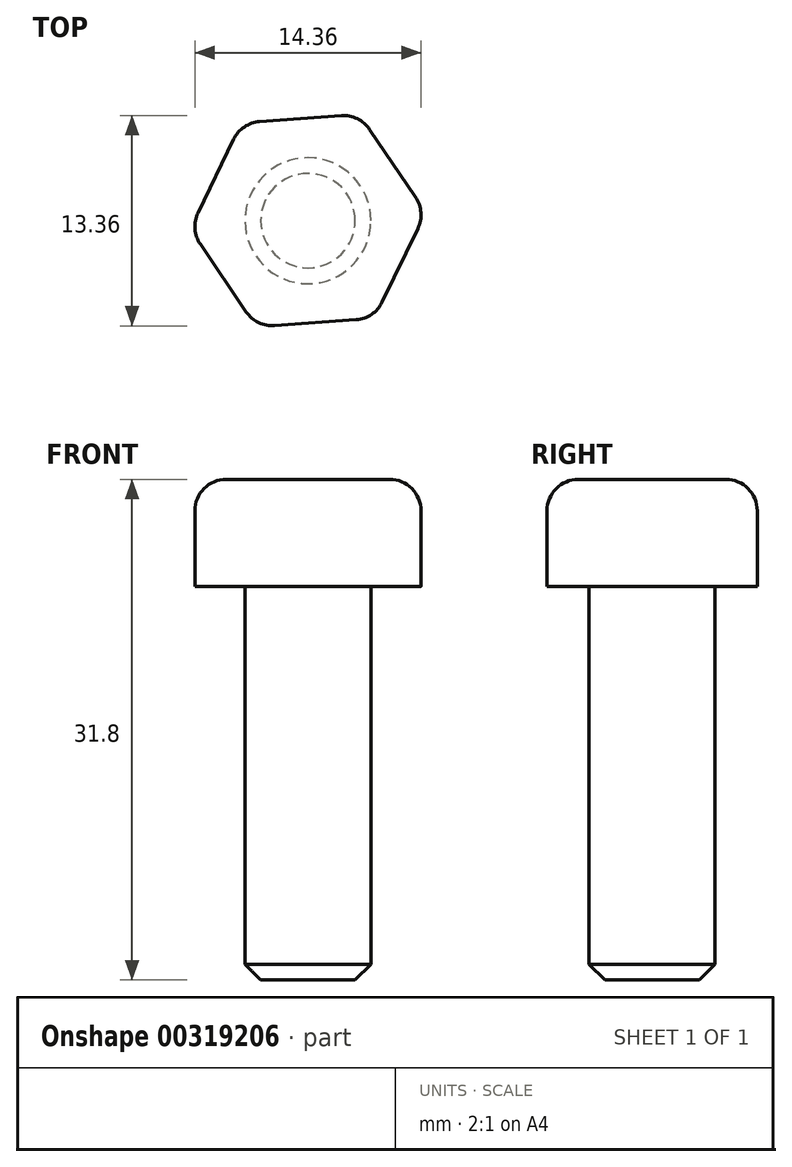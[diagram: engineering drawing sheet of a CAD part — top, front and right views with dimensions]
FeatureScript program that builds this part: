
annotation { "Feature Type Name" : "Feature", "Feature Type Description" : "" }
export const myFeature = defineFeature(function(context is Context, id is Id, definition is map)
    precondition{}
    {
        {
            var Q0;
            Q0=qCreatedBy(makeId("Top.planeOp"),FACE);
            var sketch = newSketch(context, id + "F0", { "sketchPlane" : qUnion([Q0])});
            skCircle(sketch, "E0.cCircle", {"center": v(0, 0) * mm, "radius": 6.5 * mm, "construction": true});
            skLineSegment(sketch, "E0.0", {"start": v(3.27, 6.76) * mm, "end": v(7.49, 0.54) * mm});
            skLineSegment(sketch, "E0.1", {"start": v(7.49, 0.54) * mm, "end": v(4.21, -6.21) * mm});
            skLineSegment(sketch, "E0.2", {"start": v(4.21, -6.21) * mm, "end": v(-3.27, -6.76) * mm});
            skLineSegment(sketch, "E0.3", {"start": v(-3.27, -6.76) * mm, "end": v(-7.49, -0.54) * mm});
            skLineSegment(sketch, "E0.4", {"start": v(-7.49, -0.54) * mm, "end": v(-4.21, 6.21) * mm});
            skLineSegment(sketch, "E0.5", {"start": v(-4.21, 6.21) * mm, "end": v(3.27, 6.76) * mm});
            skPoint(sketch, "E0.0.midPoint", {"position": v(5.38, 3.65) * mm});
            skSolve(sketch);
        }
        {
            var Q0;
            Q0 = qSketchRegion(id + "F0", true);
            extrude(context, id + "F1", {"entities" : qUnion([Q0]), "depth" : 6.8 * mm});
        }
        {
            var Q0;
            Q0=makeQuery(id+"F1.opExtrude","CAP_FACE",FACE,{"disambiguationData":[OSD([sQuery(id+"F0.wireOp",EDGE,"E0.0"),sQuery(id+"F0.wireOp",EDGE,"E0.1"),sQuery(id+"F0.wireOp",EDGE,"E0.2"),sQuery(id+"F0.wireOp",EDGE,"E0.3"),sQuery(id+"F0.wireOp",EDGE,"E0.4"),sQuery(id+"F0.wireOp",EDGE,"E0.5")])],"isStart":true});
            var sketch = newSketch(context, id + "F2", { "sketchPlane" : qUnion([Q0])});
            skCircle(sketch, "E1", {"center": v(0, 0) * mm, "radius": 4 * mm});
            skSolve(sketch);
        }
        {
            var Q0;
            Q0 = qSketchRegion(id + "F2", true);
            extrude(context, id + "F3", {"entities" : qUnion([Q0]), "operationType" : NewBodyOperationType.ADD, "depth" : 25 * mm});
        }
        {
            var Q0;
            Q0=makeQuery(id+"F3.opExtrude","CAP_EDGE",EDGE,{"disambiguationData":[OSD([sQuery(id+"F2.wireOp",EDGE,"E1")])],"isStart":false});
            chamfer(context, id + "F4", {"entities" : qUnion([Q0]), "width" : 1 * mm, "tangentPropagation" : true});
        }
        {
            var Q0;
            Q0=makeQuery(id+"F1.opExtrude","CAP_EDGE",EDGE,{"disambiguationData":[OSD([sQuery(id+"F0.wireOp",EDGE,"E0.2")])],"isStart":false});
            var Q1;
            Q1=makeQuery(id+"F1.opExtrude","CAP_EDGE",EDGE,{"disambiguationData":[OSD([sQuery(id+"F0.wireOp",EDGE,"E0.3")])],"isStart":false});
            var Q2;
            Q2=makeQuery(id+"F1.opExtrude","CAP_EDGE",EDGE,{"disambiguationData":[OSD([sQuery(id+"F0.wireOp",EDGE,"E0.4")])],"isStart":false});
            var Q3;
            Q3=makeQuery(id+"F1.opExtrude","CAP_EDGE",EDGE,{"disambiguationData":[OSD([sQuery(id+"F0.wireOp",EDGE,"E0.5")])],"isStart":false});
            var Q4;
            Q4=makeQuery(id+"F1.opExtrude","CAP_EDGE",EDGE,{"disambiguationData":[OSD([sQuery(id+"F0.wireOp",EDGE,"E0.0")])],"isStart":false});
            var Q5;
            Q5=makeQuery(id+"F1.opExtrude","CAP_EDGE",EDGE,{"disambiguationData":[OSD([sQuery(id+"F0.wireOp",EDGE,"E0.1")])],"isStart":false});
            var Q6;
            Q6=makeQuery(id+"F1.opExtrude","SWEPT_EDGE",EDGE,{"disambiguationData":[OSD([sQuery(id+"F0.wireOp",EDGE,"E0.0"),sQuery(id+"F0.wireOp",EDGE,"E0.1")])]});
            var Q7;
            Q7=makeQuery(id+"F1.opExtrude","SWEPT_EDGE",EDGE,{"disambiguationData":[OSD([sQuery(id+"F0.wireOp",EDGE,"E0.1"),sQuery(id+"F0.wireOp",EDGE,"E0.2")])]});
            var Q8;
            Q8=makeQuery(id+"F1.opExtrude","SWEPT_EDGE",EDGE,{"disambiguationData":[OSD([sQuery(id+"F0.wireOp",EDGE,"E0.2"),sQuery(id+"F0.wireOp",EDGE,"E0.3")])]});
            var Q9;
            Q9=makeQuery(id+"F1.opExtrude","SWEPT_EDGE",EDGE,{"disambiguationData":[OSD([sQuery(id+"F0.wireOp",EDGE,"E0.3"),sQuery(id+"F0.wireOp",EDGE,"E0.4")])]});
            var Q10;
            Q10=makeQuery(id+"F1.opExtrude","SWEPT_EDGE",EDGE,{"disambiguationData":[OSD([sQuery(id+"F0.wireOp",EDGE,"E0.4"),sQuery(id+"F0.wireOp",EDGE,"E0.5")])]});
            var Q11;
            Q11=makeQuery(id+"F1.opExtrude","SWEPT_EDGE",EDGE,{"disambiguationData":[OSD([sQuery(id+"F0.wireOp",EDGE,"E0.0"),sQuery(id+"F0.wireOp",EDGE,"E0.5")])]});
            fillet(context, id + "F5", {"entities" : qUnion([Q0, Q1, Q2, Q3, Q4, Q5, Q6, Q7, Q8, Q9, Q10, Q11]), "radius" : 2 * mm, "tangentPropagation" : true, "allowEdgeOverflow" : false});
        }
    });
